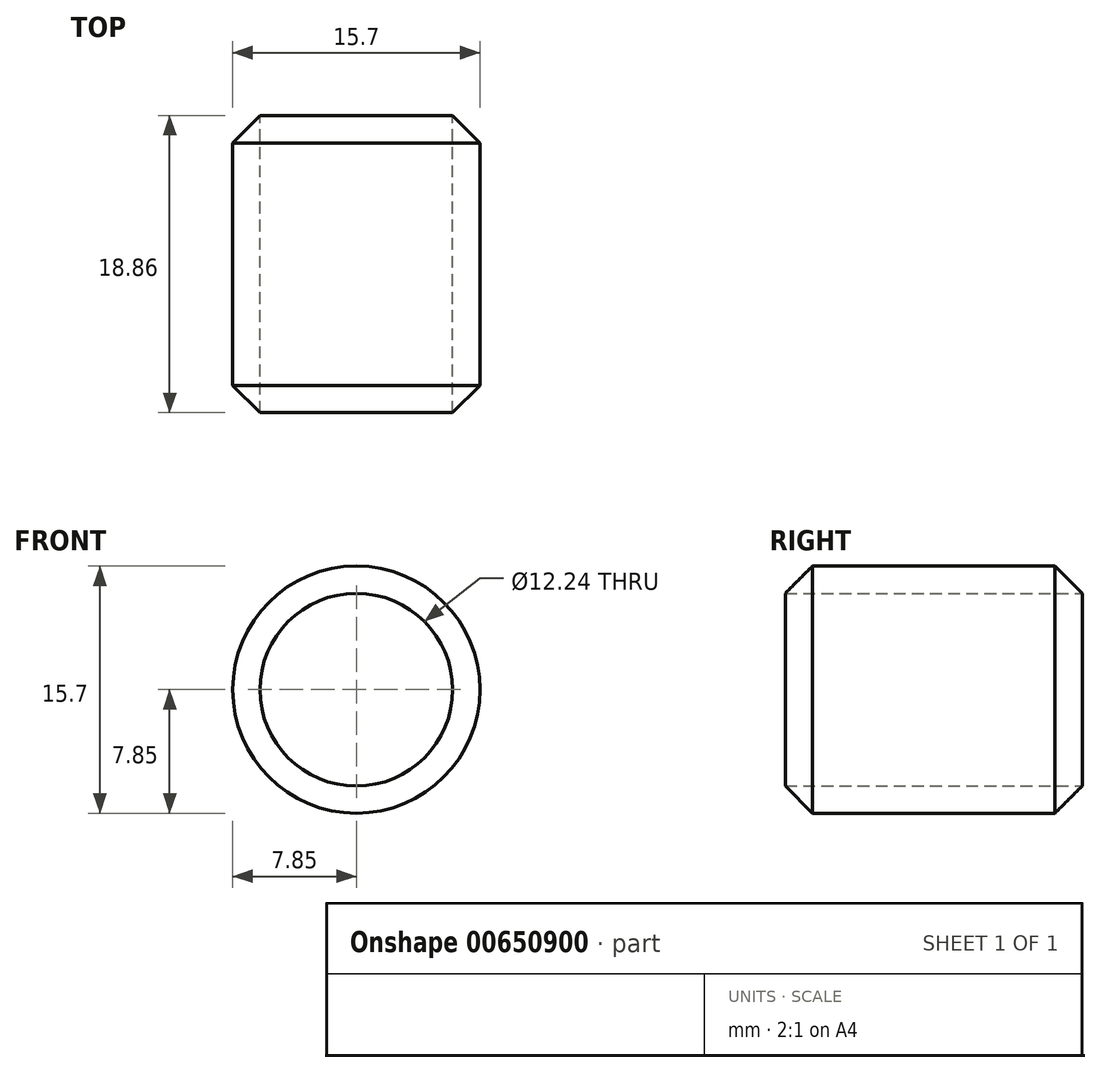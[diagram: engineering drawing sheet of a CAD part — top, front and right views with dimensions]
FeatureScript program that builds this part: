
annotation { "Feature Type Name" : "Feature", "Feature Type Description" : "" }
export const myFeature = defineFeature(function(context is Context, id is Id, definition is map)
    precondition{}
    {
        {
            var Q0;
            Q0=qCreatedBy(makeId("Front.planeOp"),FACE);
            var sketch = newSketch(context, id + "F0", { "sketchPlane" : qUnion([Q0])});
            skCircle(sketch, "E0", {"center": v(0, 0) * mm, "radius": 7.85 * mm});
            skSolve(sketch);
        }
        {
            var Q0;
            Q0=makeQuery(id+"F0.imprint","IMPRINT",FACE,{"disambiguationData":[TD([[makeQuery(id+"F0.imprint","IMPRINT",EDGE,{"derivedFrom":sQuery(id+"F0.wireOp",EDGE,"E0")}),1.0]])]});
            extrude(context, id + "F1", {"entities" : qUnion([Q0]), "depth" : 25.4 * mm, "offsetDistance" : 25 * mm});
        }
        {
            var Q0;
            Q0=makeQuery(id+"F1.opExtrude","CAP_FACE",FACE,{"disambiguationData":[OSD([sQuery(id+"F0.wireOp",EDGE,"E0")])],"isStart":true});
            var sketch = newSketch(context, id + "F2", { "sketchPlane" : qUnion([Q0])});
            skCircle(sketch, "E1", {"center": v(0, 0) * mm, "radius": 2.19 * mm});
            skSolve(sketch);
        }
        {
            var Q0;
            Q0=sQuery(id+"F2.wireOp",VERTEX,"E1.center");
            var Q1;
            Q1=makeQuery(id+"F1.opExtrude","SWEPT_BODY",BODY,{"disambiguationData":[OSD([sQuery(id+"F0.wireOp",EDGE,"E0")])]});
            hole(context, id + "F3", {"style" : HoleStyle.SIMPLE, "endStyle" : HoleEndStyle.THROUGH, "holeDiameter" : 12.24 * mm, "majorDiameter" : 5 * mm, "isTappedThrough" : true, "tappedDepth" : 12 * mm, "tapClearance" : 3, "locations" : qUnion([Q0]), "scope" : qUnion([Q1])});
        }
        {
            var Q0;
            Q0=makeQuery(id+"F1.opExtrude","CAP_EDGE",EDGE,{"disambiguationData":[OSD([sQuery(id+"F0.wireOp",EDGE,"E0")])],"isStart":true});
            chamfer(context, id + "F4", {"entities" : qUnion([Q0]), "width" : 5 * mm, "tangentPropagation" : true});
        }
        {
            var Q0;
            Q0=makeQuery(id+"F1.opExtrude","CAP_EDGE",EDGE,{"disambiguationData":[OSD([sQuery(id+"F0.wireOp",EDGE,"E0")])],"isStart":false});
            chamfer(context, id + "F5", {"entities" : qUnion([Q0]), "width" : 5 * mm, "tangentPropagation" : true});
        }
    });
